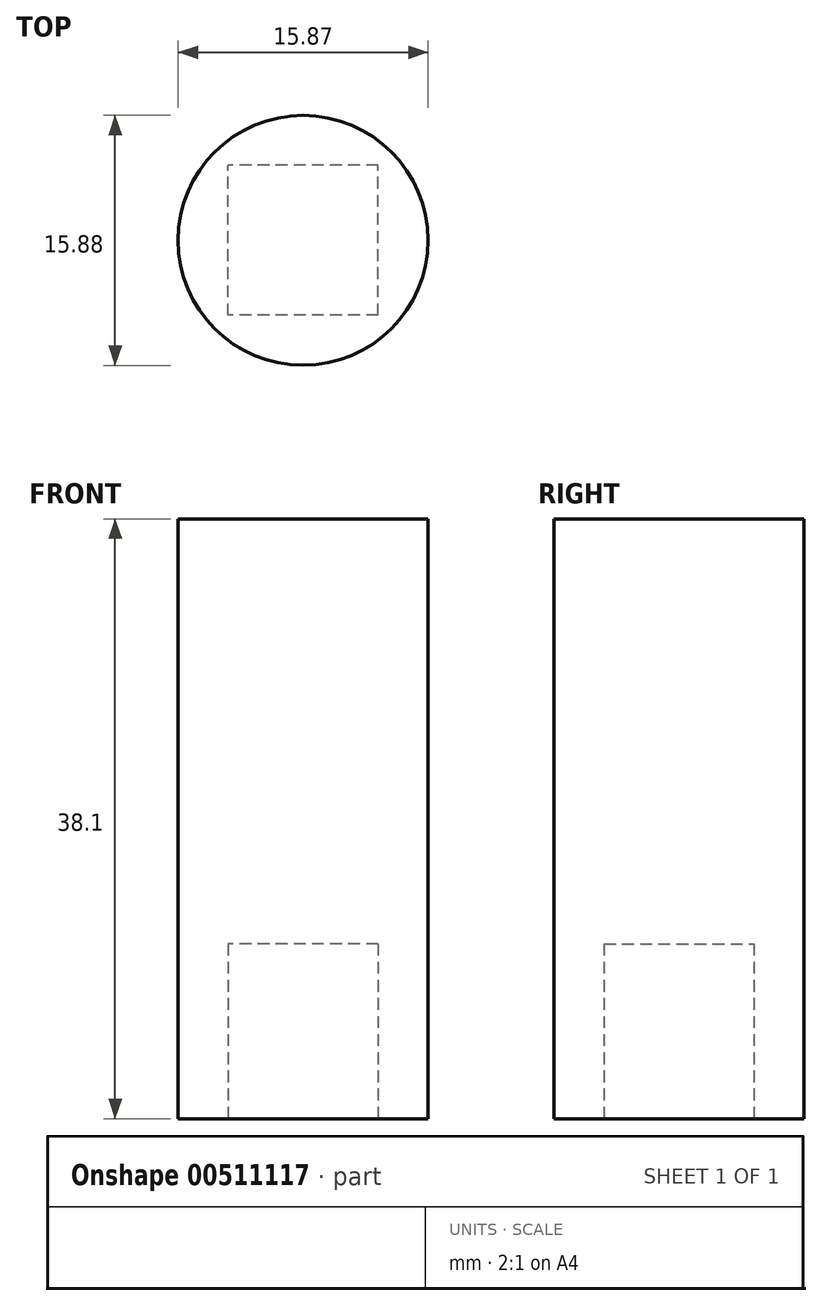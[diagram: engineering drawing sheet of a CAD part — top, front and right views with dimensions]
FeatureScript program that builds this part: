
annotation { "Feature Type Name" : "Feature", "Feature Type Description" : "" }
export const myFeature = defineFeature(function(context is Context, id is Id, definition is map)
    precondition{}
    {
        {
            var Q0;
            Q0=qCreatedBy(makeId("Front.planeOp"),FACE);
            var sketch = newSketch(context, id + "F0", { "sketchPlane" : qUnion([Q0])});
            skLineSegment(sketch, "E0.bottom", {"start": v(-29.33, 22.16) * mm, "end": v(-21.4, 22.16) * mm});
            skLineSegment(sketch, "E0.top", {"start": v(-29.33, -15.94) * mm, "end": v(-21.4, -15.94) * mm});
            skLineSegment(sketch, "E0.left", {"start": v(-29.33, 22.16) * mm, "end": v(-29.33, -15.94) * mm});
            skLineSegment(sketch, "E0.right", {"start": v(-21.4, 22.16) * mm, "end": v(-21.4, -15.94) * mm});
            skSolve(sketch);
        }
        {
            var Q0;
            Q0=makeQuery(id+"F0.imprint","IMPRINT",FACE,{"disambiguationData":[TD([[makeQuery(id+"F0.imprint","IMPRINT",EDGE,{"derivedFrom":sQuery(id+"F0.wireOp",EDGE,"E0.bottom")}),-1.0]])]});
            var Q1;
            Q1=sQuery(id+"F0.wireOp",EDGE,"E0.right");
            revolve(context, id + "F1", {"entities" : qUnion([Q0]), "axis" : qUnion([Q1]), "revolveType" : RevolveType.FULL});
        }
        {
            var Q0;
            Q0=makeQuery(id+"F1.opRevolve","SWEPT_FACE",FACE,{"disambiguationData":[OSD([sQuery(id+"F0.wireOp",EDGE,"E0.top")])]});
            var sketch = newSketch(context, id + "F2", { "sketchPlane" : qUnion([Q0])});
            skPoint(sketch, "E1", {"position": v(-21.4, 0) * mm});
            skPoint(sketch, "E2", {"position": v(-16.63, 0) * mm});
            skPoint(sketch, "E3", {"position": v(-21.4, -4.78) * mm});
            skLineSegment(sketch, "E4.bottom", {"start": v(-16.63, 4.76) * mm, "end": v(-26.16, 4.76) * mm});
            skLineSegment(sketch, "E4.top", {"start": v(-16.63, -4.76) * mm, "end": v(-26.16, -4.76) * mm});
            skLineSegment(sketch, "E4.left", {"start": v(-16.63, 4.76) * mm, "end": v(-16.63, -4.76) * mm});
            skLineSegment(sketch, "E4.right", {"start": v(-26.16, 4.76) * mm, "end": v(-26.16, -4.76) * mm});
            skSolve(sketch);
        }
        {
            var Q0;
            Q0=makeQuery(id+"F2.imprint","IMPRINT",FACE,{"disambiguationData":[TD([[makeQuery(id+"F2.imprint","IMPRINT",EDGE,{"derivedFrom":sQuery(id+"F2.wireOp",EDGE,"E4.bottom")}),1.0]])]});
            extrude(context, id + "F3", {"entities" : qUnion([Q0]), "operationType" : NewBodyOperationType.REMOVE, "oppositeDirection" : true, "depth" : 11.1 * mm});
        }
    });
